# Revit family: Haworth_ActiveComponents_RectangleConvergentConferenceEnd_BUILD
name_source: partatom
category: Furniture Systems
revit_build: Autodesk Revit Architecture 2015 (Build: 20141119_1515(x64)
units: mm (PartAtom-declared; Revit-internal decimal feet)

## types (4) — shared parameters
Actual Height = 29 3/16"
Angled Leg Offset = 3 9/16"
Assembly Code = E2020200
Custom Size = No
Description = Haworth - Active Components - Rectangle Convergent Conference End
Leg F/B Offset = 8"
Manufacturer = Haworth
Max. Depth = 30"
Max. Width = 72"
Min. Depth = 24"
Min. Width = 60"
Model = WAYG
Radius = 3"
Revision Number = 1
Size = Verify Final Dim. w/ Haworth
Thickness = 1 3/16"
URL = www.haworth.com
URL - Product = https://www.haworth.com
Warranty = https://www.haworth.com
With Leg = Yes

## per-type parameters (varying)
| type | Actual Depth | Actual Width | Depth | Width |
| 30d 72w | 30" | 72" | 30" | 72" |
| 30d 60w | 30" | 60" | 30" | 60" |
| 24d 72w | 24" | 72" | 24" | 72" |
| 24d 60w | 24" | 60" | 24" | 60" |

## geometry (parser evidence)
native form markers: Blend x49, Sweep x5
no freeform markers — native parametric forms only
